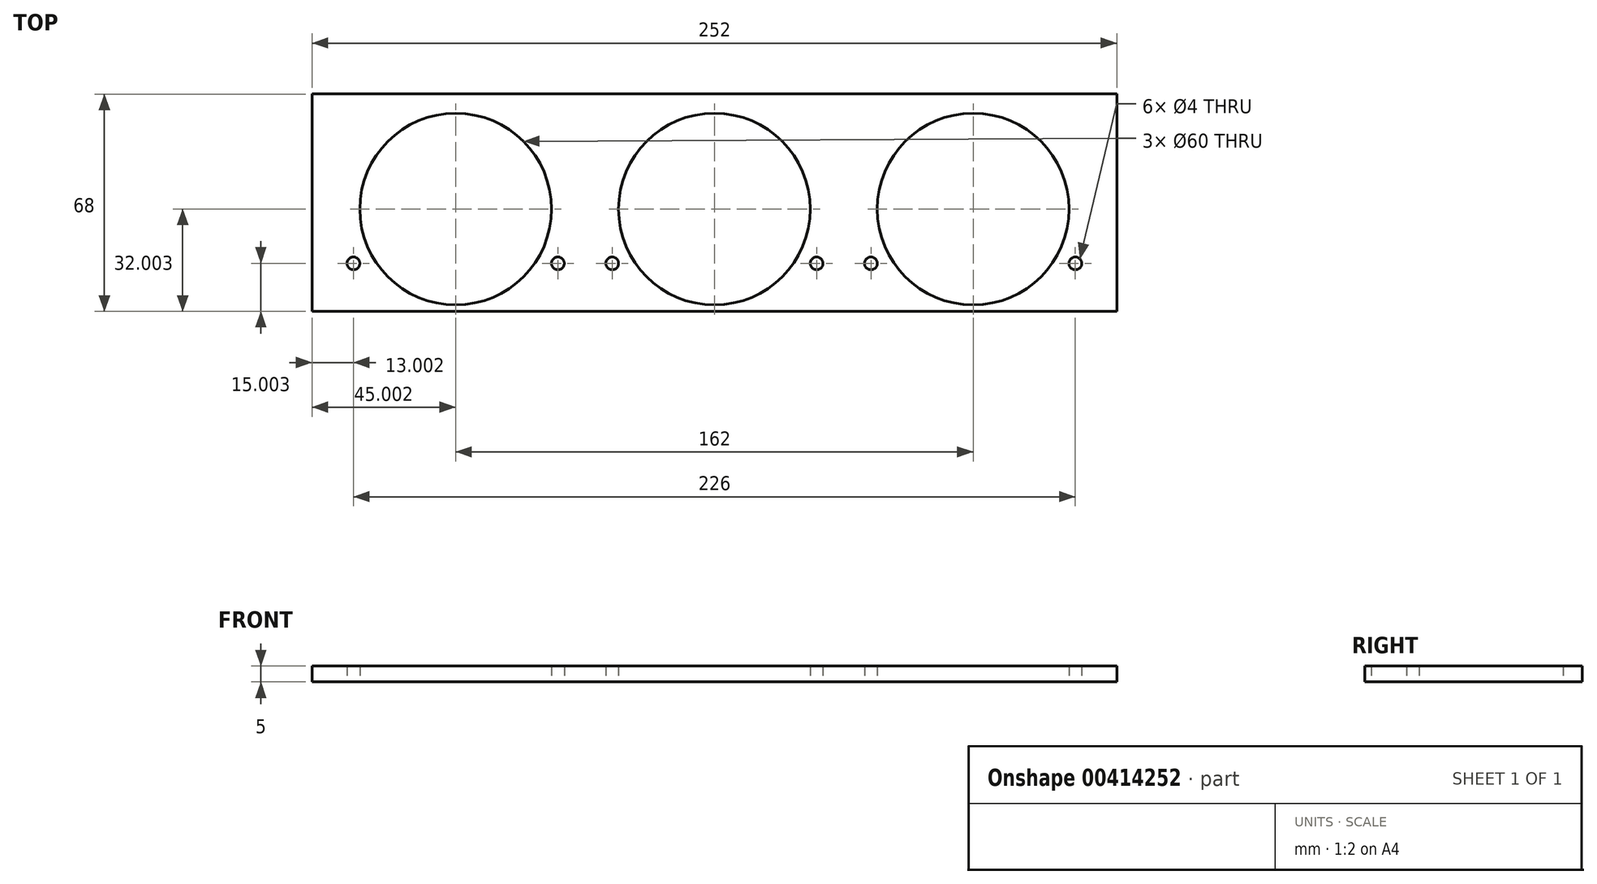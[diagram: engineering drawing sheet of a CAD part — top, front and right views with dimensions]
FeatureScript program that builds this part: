
annotation { "Feature Type Name" : "Feature", "Feature Type Description" : "" }
export const myFeature = defineFeature(function(context is Context, id is Id, definition is map)
    precondition{}
    {
        {
            var Q0;
            Q0=qCreatedBy(makeId("Top.planeOp"),FACE);
            var sketch = newSketch(context, id + "F0", { "sketchPlane" : qUnion([Q0])});
            skCircle(sketch, "E0", {"center": v(-36.45, 12.97) * mm, "radius": 30 * mm});
            skCircle(sketch, "E1", {"center": v(-4.45, -4.03) * mm, "radius": 2 * mm});
            skCircle(sketch, "E2", {"center": v(-68.45, -4.03) * mm, "radius": 2 * mm});
            skCircle(sketch, "E3", {"center": v(44.55, 12.97) * mm, "radius": 30 * mm});
            skCircle(sketch, "E4", {"center": v(76.55, -4.03) * mm, "radius": 2 * mm});
            skCircle(sketch, "E5", {"center": v(12.55, -4.03) * mm, "radius": 2 * mm});
            skCircle(sketch, "E6", {"center": v(-117.45, 12.97) * mm, "radius": 30 * mm});
            skCircle(sketch, "E7", {"center": v(-85.45, -4.03) * mm, "radius": 2 * mm});
            skCircle(sketch, "E8", {"center": v(-149.45, -4.03) * mm, "radius": 2 * mm});
            skLineSegment(sketch, "E9.bottom", {"start": v(-162.45, -19.03) * mm, "end": v(89.55, -19.03) * mm});
            skLineSegment(sketch, "E9.top", {"start": v(-162.45, 48.97) * mm, "end": v(89.55, 48.97) * mm});
            skLineSegment(sketch, "E9.left", {"start": v(-162.45, -19.03) * mm, "end": v(-162.45, 48.97) * mm});
            skLineSegment(sketch, "E9.right", {"start": v(89.55, -19.03) * mm, "end": v(89.55, 48.97) * mm});
            skSolve(sketch);
        }
        {
            var Q0;
            Q0=makeQuery(id+"F0.imprint","IMPRINT",FACE,{"disambiguationData":[TD([[makeQuery(id+"F0.imprint","IMPRINT",EDGE,{"derivedFrom":sQuery(id+"F0.wireOp",EDGE,"E0")}),-1.0]])]});
            extrude(context, id + "F1", {"entities" : qUnion([Q0]), "depth" : 5 * mm, "offsetDistance" : 25 * mm});
        }
    });
